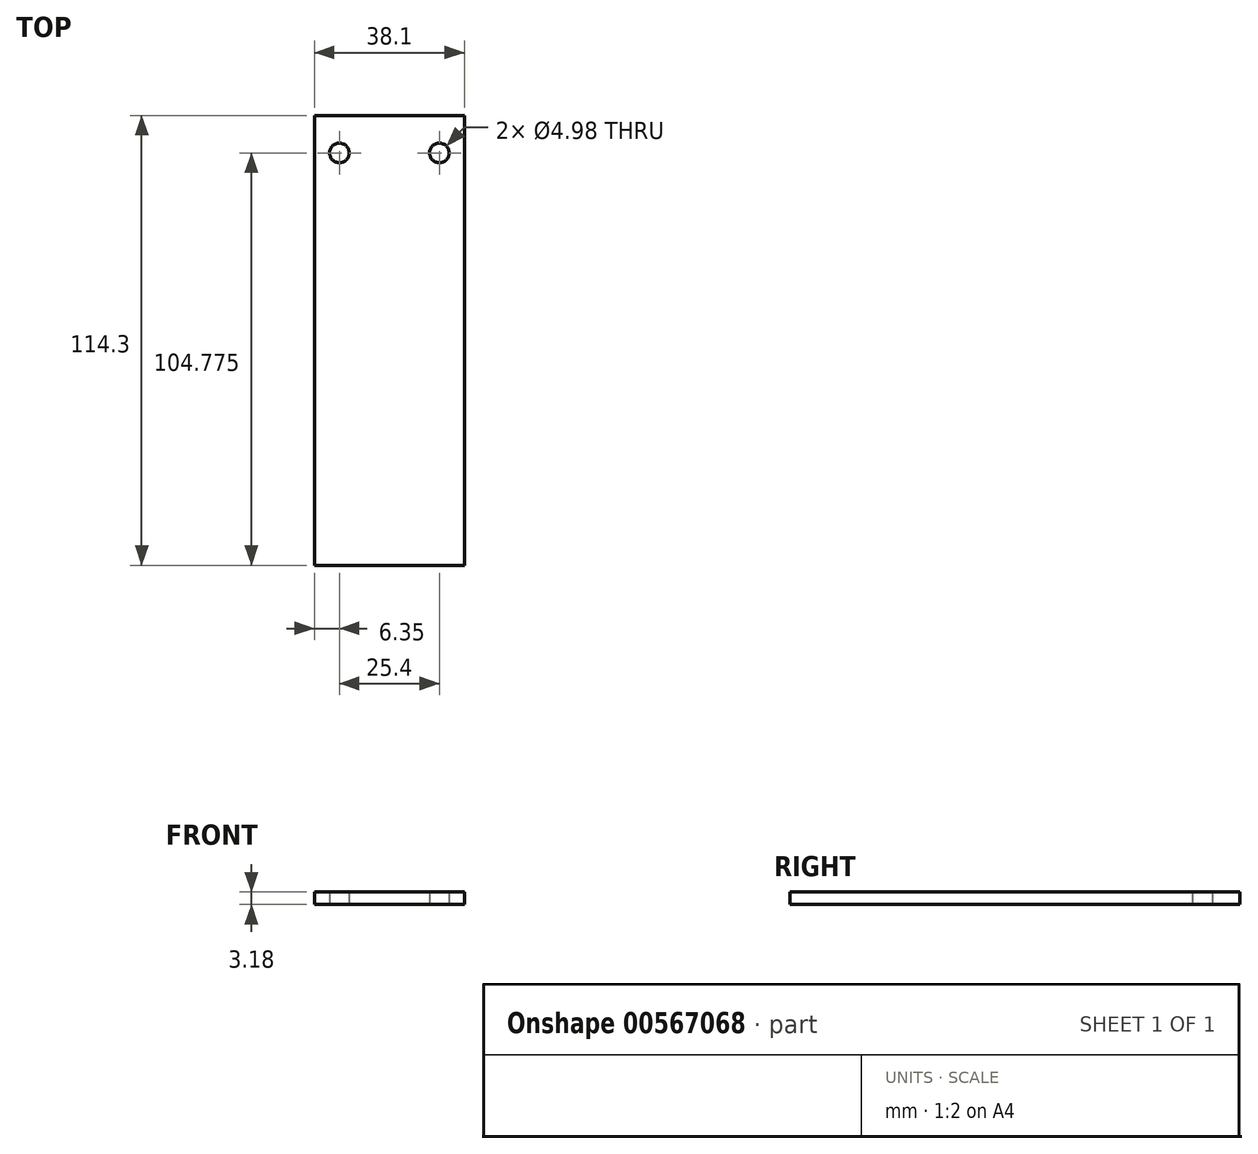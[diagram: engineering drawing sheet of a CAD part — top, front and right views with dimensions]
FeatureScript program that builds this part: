
annotation { "Feature Type Name" : "Feature", "Feature Type Description" : "" }
export const myFeature = defineFeature(function(context is Context, id is Id, definition is map)
    precondition{}
    {
        {
            var Q0;
            Q0=qCreatedBy(makeId("Top.planeOp"),FACE);
            var sketch = newSketch(context, id + "F0", { "sketchPlane" : qUnion([Q0])});
            skLineSegment(sketch, "E0.bottom", {"start": v(-19.05, 57.15) * mm, "end": v(19.05, 57.15) * mm});
            skLineSegment(sketch, "E0.top", {"start": v(-19.05, -57.15) * mm, "end": v(19.05, -57.15) * mm});
            skLineSegment(sketch, "E0.left", {"start": v(-19.05, 57.15) * mm, "end": v(-19.05, -57.15) * mm});
            skLineSegment(sketch, "E0.right", {"start": v(19.05, 57.15) * mm, "end": v(19.05, -57.15) * mm});
            skPoint(sketch, "E0.middle", {"position": v(0, 0) * mm});
            skCircle(sketch, "E1", {"center": v(-12.7, 47.62) * mm, "radius": 2.49 * mm});
            skCircle(sketch, "E2.MirrorC", {"center": v(12.7, 47.62) * mm, "radius": 2.49 * mm});
            skSolve(sketch);
        }
        {
            var Q0;
            Q0=makeQuery(id+"F0.imprint","IMPRINT",FACE,{"disambiguationData":[TD([[makeQuery(id+"F0.imprint","IMPRINT",EDGE,{"derivedFrom":sQuery(id+"F0.wireOp",EDGE,"E0.bottom")}),-1.0]])]});
            extrude(context, id + "F1", {"entities" : qUnion([Q0]), "depth" : 3.17 * mm});
        }
    });
